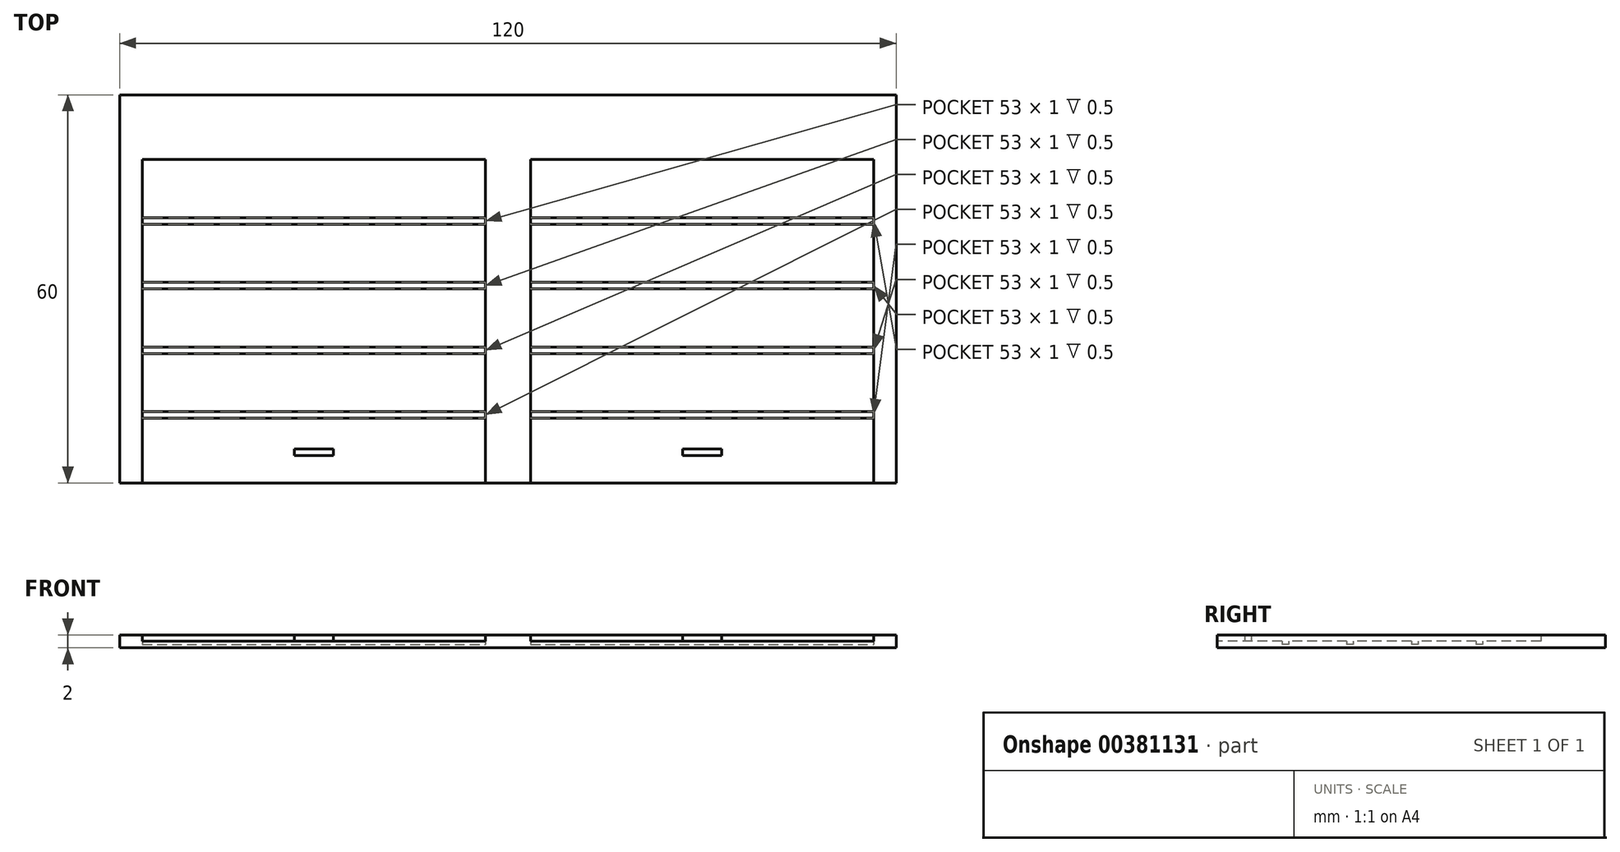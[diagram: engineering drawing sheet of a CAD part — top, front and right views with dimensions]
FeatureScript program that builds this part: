
annotation { "Feature Type Name" : "Feature", "Feature Type Description" : "" }
export const myFeature = defineFeature(function(context is Context, id is Id, definition is map)
    precondition{}
    {
        {
            var Q0;
            Q0=qCreatedBy(makeId("Top.planeOp"),FACE);
            var sketch = newSketch(context, id + "F0", { "sketchPlane" : qUnion([Q0])});
            skLineSegment(sketch, "E0.bottom", {"start": v(60, -30) * mm, "end": v(-60, -30) * mm});
            skLineSegment(sketch, "E0.top", {"start": v(60, 30) * mm, "end": v(-60, 30) * mm});
            skLineSegment(sketch, "E0.left", {"start": v(60, -30) * mm, "end": v(60, 30) * mm});
            skLineSegment(sketch, "E0.right", {"start": v(-60, -30) * mm, "end": v(-60, 30) * mm});
            skPoint(sketch, "E0.middle", {"position": v(0, 0) * mm});
            skLineSegment(sketch, "E1.bottom", {"start": v(-56.5, 20) * mm, "end": v(-3.5, 20) * mm});
            skLineSegment(sketch, "E2.bottom", {"start": v(-56.5, 11) * mm, "end": v(-3.5, 11) * mm});
            skLineSegment(sketch, "E2.top", {"start": v(-56.5, 10) * mm, "end": v(-3.5, 10) * mm});
            skLineSegment(sketch, "E3.bottom", {"start": v(-56.5, 1) * mm, "end": v(-3.5, 1) * mm});
            skLineSegment(sketch, "E3.top", {"start": v(-56.5, 0) * mm, "end": v(-3.5, 0) * mm});
            skLineSegment(sketch, "E4.bottom", {"start": v(-56.5, -9) * mm, "end": v(-3.5, -9) * mm});
            skLineSegment(sketch, "E4.top", {"start": v(-56.5, -10) * mm, "end": v(-3.5, -10) * mm});
            skLineSegment(sketch, "E5.bottom", {"start": v(-56.5, -19) * mm, "end": v(-3.5, -19) * mm});
            skLineSegment(sketch, "E5.top", {"start": v(-56.5, -20) * mm, "end": v(-3.5, -20) * mm});
            skLineSegment(sketch, "E6.bottom", {"start": v(-33, -24.77) * mm, "end": v(-27, -24.77) * mm});
            skLineSegment(sketch, "E6.top", {"start": v(-33, -25.77) * mm, "end": v(-27, -25.77) * mm});
            skLineSegment(sketch, "E6.left", {"start": v(-33, -24.77) * mm, "end": v(-33, -25.77) * mm});
            skLineSegment(sketch, "E6.right", {"start": v(-27, -24.77) * mm, "end": v(-27, -25.77) * mm});
            skLineSegment(sketch, "E7", {"start": v(-56.5, 20) * mm, "end": v(-56.5, -30) * mm});
            skLineSegment(sketch, "E8", {"start": v(-3.5, 20) * mm, "end": v(-3.5, -30) * mm});
            skLineSegment(sketch, "E9.1.0.0", {"start": v(3.5, -19) * mm, "end": v(56.5, -19) * mm});
            skLineSegment(sketch, "E9.1.0.1", {"start": v(3.5, 20) * mm, "end": v(56.5, 20) * mm});
            skLineSegment(sketch, "E9.1.0.2", {"start": v(3.5, -9) * mm, "end": v(56.5, -9) * mm});
            skLineSegment(sketch, "E9.1.0.3", {"start": v(3.5, -10) * mm, "end": v(56.5, -10) * mm});
            skLineSegment(sketch, "E9.1.0.4", {"start": v(3.5, 1) * mm, "end": v(56.5, 1) * mm});
            skLineSegment(sketch, "E9.1.0.5", {"start": v(3.5, 11) * mm, "end": v(56.5, 11) * mm});
            skLineSegment(sketch, "E9.1.0.6", {"start": v(3.5, 10) * mm, "end": v(56.5, 10) * mm});
            skLineSegment(sketch, "E9.1.0.7", {"start": v(56.5, 20) * mm, "end": v(56.5, -30) * mm});
            skLineSegment(sketch, "E9.1.0.8", {"start": v(3.5, 0) * mm, "end": v(56.5, 0) * mm});
            skLineSegment(sketch, "E9.1.0.9", {"start": v(3.5, -20) * mm, "end": v(56.5, -20) * mm});
            skLineSegment(sketch, "E9.1.0.10", {"start": v(3.5, 20) * mm, "end": v(3.5, -30) * mm});
            skLineSegment(sketch, "E9.1.0.11", {"start": v(27, -25.77) * mm, "end": v(33, -25.77) * mm});
            skLineSegment(sketch, "E9.1.0.12", {"start": v(27, -24.77) * mm, "end": v(33, -24.77) * mm});
            skLineSegment(sketch, "E9.1.0.13", {"start": v(33, -24.77) * mm, "end": v(33, -25.77) * mm});
            skLineSegment(sketch, "E9.1.0.14", {"start": v(27, -24.77) * mm, "end": v(27, -25.77) * mm});
            skLineSegment(sketch, "E9.direction1", {"start": v(-56.5, -30) * mm, "end": v(3.5, -30) * mm, "construction": true});
            skSolve(sketch);
        }
        {
            var Q0;
            Q0=makeQuery(id+"F0.imprint","IMPRINT",FACE,{"disambiguationData":[TD([[makeQuery(id+"F0.imprint","IMPRINT",EDGE,{"derivedFrom":sQuery(id+"F0.wireOp",EDGE,"E0.top")}),1.0]])]});
            extrude(context, id + "F1", {"entities" : qUnion([Q0]), "depth" : 2 * mm});
        }
        {
            var Q0;
            {var subQ0=sQuery(id+"F0.wireOp",EDGE,"E1.bottom");Q0=makeQuery(id+"F0.imprint","IMPRINT",FACE,{"disambiguationData":[TD([[makeQuery(id+"F0.imprint","IMPRINT",EDGE,{"derivedFrom":subQ0}),-1.0]])]});}
            var Q1;
            {var subQ0=sQuery(id+"F0.wireOp",EDGE,"E2.top");Q1=makeQuery(id+"F0.imprint","IMPRINT",FACE,{"disambiguationData":[TD([[makeQuery(id+"F0.imprint","IMPRINT",EDGE,{"derivedFrom":subQ0}),-1.0]])]});}
            var Q2;
            {var subQ0=sQuery(id+"F0.wireOp",EDGE,"E3.top");Q2=makeQuery(id+"F0.imprint","IMPRINT",FACE,{"disambiguationData":[TD([[makeQuery(id+"F0.imprint","IMPRINT",EDGE,{"derivedFrom":subQ0}),-1.0]])]});}
            var Q3;
            {var subQ0=sQuery(id+"F0.wireOp",EDGE,"E4.top");Q3=makeQuery(id+"F0.imprint","IMPRINT",FACE,{"disambiguationData":[TD([[makeQuery(id+"F0.imprint","IMPRINT",EDGE,{"derivedFrom":subQ0}),-1.0]])]});}
            var Q4;
            {var subQ0=sQuery(id+"F0.wireOp",EDGE,"E5.top");Q4=makeQuery(id+"F0.imprint","IMPRINT",FACE,{"disambiguationData":[TD([[makeQuery(id+"F0.imprint","IMPRINT",EDGE,{"derivedFrom":subQ0}),-1.0]])]});}
            var Q5;
            {var subQ1=sQuery(id+"F0.wireOp",EDGE,"E9.1.0.9");Q5=makeQuery(id+"F0.imprint","IMPRINT",FACE,{"disambiguationData":[TD([[makeQuery(id+"F0.imprint","IMPRINT",EDGE,{"derivedFrom":subQ1}),-1.0]])]});}
            var Q6;
            {var subQ0=sQuery(id+"F0.wireOp",EDGE,"E9.1.0.0");Q6=makeQuery(id+"F0.imprint","IMPRINT",FACE,{"disambiguationData":[TD([[makeQuery(id+"F0.imprint","IMPRINT",EDGE,{"derivedFrom":subQ0}),1.0]])]});}
            var Q7;
            {var subQ0=sQuery(id+"F0.wireOp",EDGE,"E9.1.0.2");Q7=makeQuery(id+"F0.imprint","IMPRINT",FACE,{"disambiguationData":[TD([[makeQuery(id+"F0.imprint","IMPRINT",EDGE,{"derivedFrom":subQ0}),1.0]])]});}
            var Q8;
            {var subQ0=sQuery(id+"F0.wireOp",EDGE,"E9.1.0.4");Q8=makeQuery(id+"F0.imprint","IMPRINT",FACE,{"disambiguationData":[TD([[makeQuery(id+"F0.imprint","IMPRINT",EDGE,{"derivedFrom":subQ0}),1.0]])]});}
            var Q9;
            {var subQ0=sQuery(id+"F0.wireOp",EDGE,"E9.1.0.1");Q9=makeQuery(id+"F0.imprint","IMPRINT",FACE,{"disambiguationData":[TD([[makeQuery(id+"F0.imprint","IMPRINT",EDGE,{"derivedFrom":subQ0}),-1.0]])]});}
            extrude(context, id + "F2", {"entities" : qUnion([Q0, Q1, Q2, Q3, Q4, Q5, Q6, Q7, Q8, Q9]), "operationType" : NewBodyOperationType.ADD, "depth" : 1 * mm});
        }
        {
            var Q0;
            {var subQ0=sQuery(id+"F0.wireOp",EDGE,"E2.bottom");Q0=makeQuery(id+"F0.imprint","IMPRINT",FACE,{"disambiguationData":[TD([[makeQuery(id+"F0.imprint","IMPRINT",EDGE,{"derivedFrom":subQ0}),-1.0]])]});}
            var Q1;
            {var subQ0=sQuery(id+"F0.wireOp",EDGE,"E3.bottom");Q1=makeQuery(id+"F0.imprint","IMPRINT",FACE,{"disambiguationData":[TD([[makeQuery(id+"F0.imprint","IMPRINT",EDGE,{"derivedFrom":subQ0}),-1.0]])]});}
            var Q2;
            {var subQ0=sQuery(id+"F0.wireOp",EDGE,"E4.bottom");Q2=makeQuery(id+"F0.imprint","IMPRINT",FACE,{"disambiguationData":[TD([[makeQuery(id+"F0.imprint","IMPRINT",EDGE,{"derivedFrom":subQ0}),-1.0]])]});}
            var Q3;
            {var subQ0=sQuery(id+"F0.wireOp",EDGE,"E5.bottom");Q3=makeQuery(id+"F0.imprint","IMPRINT",FACE,{"disambiguationData":[TD([[makeQuery(id+"F0.imprint","IMPRINT",EDGE,{"derivedFrom":subQ0}),-1.0]])]});}
            var Q4;
            {var subQ0=sQuery(id+"F0.wireOp",EDGE,"E9.1.0.0");Q4=makeQuery(id+"F0.imprint","IMPRINT",FACE,{"disambiguationData":[TD([[makeQuery(id+"F0.imprint","IMPRINT",EDGE,{"derivedFrom":subQ0}),-1.0]])]});}
            var Q5;
            {var subQ0=sQuery(id+"F0.wireOp",EDGE,"E9.1.0.2");Q5=makeQuery(id+"F0.imprint","IMPRINT",FACE,{"disambiguationData":[TD([[makeQuery(id+"F0.imprint","IMPRINT",EDGE,{"derivedFrom":subQ0}),-1.0]])]});}
            var Q6;
            {var subQ0=sQuery(id+"F0.wireOp",EDGE,"E9.1.0.4");Q6=makeQuery(id+"F0.imprint","IMPRINT",FACE,{"disambiguationData":[TD([[makeQuery(id+"F0.imprint","IMPRINT",EDGE,{"derivedFrom":subQ0}),-1.0]])]});}
            var Q7;
            {var subQ0=sQuery(id+"F0.wireOp",EDGE,"E9.1.0.5");Q7=makeQuery(id+"F0.imprint","IMPRINT",FACE,{"disambiguationData":[TD([[makeQuery(id+"F0.imprint","IMPRINT",EDGE,{"derivedFrom":subQ0}),-1.0]])]});}
            extrude(context, id + "F3", {"entities" : qUnion([Q0, Q1, Q2, Q3, Q4, Q5, Q6, Q7]), "operationType" : NewBodyOperationType.ADD, "depth" : .5 * mm});
        }
        {
            var Q0;
            Q0=makeQuery(id+"F0.imprint","IMPRINT",FACE,{"disambiguationData":[TD([[makeQuery(id+"F0.imprint","IMPRINT",EDGE,{"derivedFrom":sQuery(id+"F0.wireOp",EDGE,"E6.bottom")}),-1.0]])]});
            var Q1;
            Q1=makeQuery(id+"F0.imprint","IMPRINT",FACE,{"disambiguationData":[TD([[makeQuery(id+"F0.imprint","IMPRINT",EDGE,{"derivedFrom":sQuery(id+"F0.wireOp",EDGE,"E9.1.0.11")}),1.0]])]});
            extrude(context, id + "F4", {"entities" : qUnion([Q0, Q1]), "operationType" : NewBodyOperationType.ADD, "depth" : 2 * mm});
        }
    });
